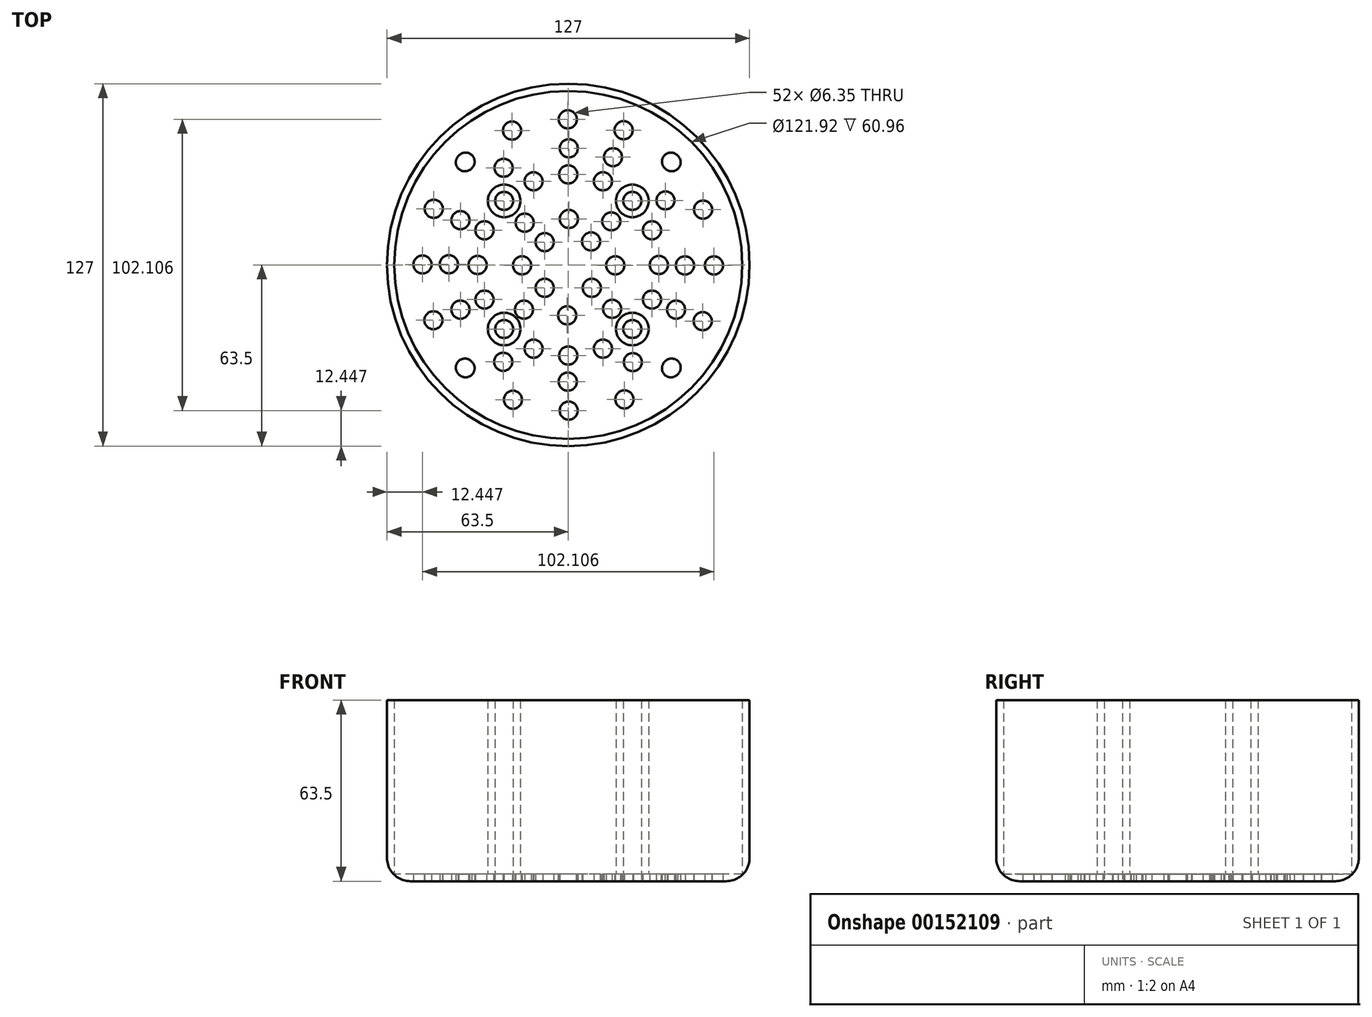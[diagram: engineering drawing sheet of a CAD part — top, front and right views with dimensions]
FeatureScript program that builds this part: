
annotation { "Feature Type Name" : "Feature", "Feature Type Description" : "" }
export const myFeature = defineFeature(function(context is Context, id is Id, definition is map)
    precondition{}
    {
        {
            var Q0;
            Q0=qCreatedBy(makeId("Top.planeOp"),FACE);
            var sketch = newSketch(context, id + "F0", { "sketchPlane" : qUnion([Q0])});
            skCircle(sketch, "E0", {"center": v(0, 0) * mm, "radius": 63.5 * mm});
            skLineSegment(sketch, "E1", {"start": v(0, 0) * mm, "end": v(-63.5, 0) * mm, "construction": true});
            skLineSegment(sketch, "E2", {"start": v(-63.5, 0) * mm, "end": v(0, 0) * mm, "construction": true});
            skLineSegment(sketch, "E3", {"start": v(0, 0) * mm, "end": v(-44.9, 44.9) * mm, "construction": true});
            skCircle(sketch, "E4", {"center": v(-22.45, 22.45) * mm, "radius": 3.18 * mm});
            skCircle(sketch, "E5", {"center": v(-36.22, 35.98) * mm, "radius": 3.18 * mm});
            skCircle(sketch, "E6", {"center": v(-8.25, 8.02) * mm, "radius": 3.18 * mm});
            skCircle(sketch, "E7.MirrorC", {"center": v(-8.25, -8.02) * mm, "radius": 3.18 * mm});
            skCircle(sketch, "E8.MirrorC", {"center": v(-36.22, -35.98) * mm, "radius": 3.18 * mm});
            skCircle(sketch, "E9.MirrorC", {"center": v(-22.45, -22.45) * mm, "radius": 3.18 * mm});
            skCircle(sketch, "E10.MirrorC", {"center": v(8.02, 8.25) * mm, "radius": 3.18 * mm});
            skCircle(sketch, "E11.MirrorC", {"center": v(22.45, 22.45) * mm, "radius": 3.18 * mm});
            skLineSegment(sketch, "E12.MirrorCS", {"start": v(0, 0) * mm, "end": v(-44.9, -44.9) * mm, "construction": true});
            skLineSegment(sketch, "E13.MirrorCS", {"start": v(0, 0) * mm, "end": v(44.9, -44.9) * mm, "construction": true});
            skLineSegment(sketch, "E14.MirrorCS", {"start": v(0, 0) * mm, "end": v(44.9, 44.9) * mm, "construction": true});
            skCircle(sketch, "E15.MirrorC", {"center": v(36.22, 35.98) * mm, "radius": 3.18 * mm});
            skCircle(sketch, "E16.MirrorC", {"center": v(36.22, -35.98) * mm, "radius": 3.18 * mm});
            skCircle(sketch, "E17.MirrorC", {"center": v(22.45, -22.45) * mm, "radius": 3.18 * mm});
            skCircle(sketch, "E18.MirrorC", {"center": v(8.25, -8.02) * mm, "radius": 3.18 * mm});
            skCircle(sketch, "E19.1.0", {"center": v(-19.69, 47.1) * mm, "radius": 3.18 * mm});
            skCircle(sketch, "E19.1.1", {"center": v(-12.15, 29.33) * mm, "radius": 3.18 * mm});
            skCircle(sketch, "E19.1.2", {"center": v(29.33, 12.15) * mm, "radius": 3.18 * mm});
            skCircle(sketch, "E19.1.3", {"center": v(47.23, 19.39) * mm, "radius": 3.18 * mm});
            skCircle(sketch, "E19.1.4", {"center": v(12.15, -29.33) * mm, "radius": 3.18 * mm});
            skCircle(sketch, "E19.1.5", {"center": v(19.69, -47.1) * mm, "radius": 3.18 * mm});
            skCircle(sketch, "E19.1.6", {"center": v(-47.23, -19.39) * mm, "radius": 3.18 * mm});
            skCircle(sketch, "E19.1.7", {"center": v(-29.33, -12.15) * mm, "radius": 3.18 * mm});
            skCircle(sketch, "E19.2.0", {"center": v(-0.16, 51.05) * mm, "radius": 3.18 * mm});
            skCircle(sketch, "E19.2.1", {"center": v(0, 31.75) * mm, "radius": 3.18 * mm});
            skCircle(sketch, "E19.2.2", {"center": v(31.75, 0) * mm, "radius": 3.18 * mm});
            skCircle(sketch, "E19.2.3", {"center": v(51.05, -0.16) * mm, "radius": 3.18 * mm});
            skCircle(sketch, "E19.2.4", {"center": v(0, -31.75) * mm, "radius": 3.18 * mm});
            skCircle(sketch, "E19.2.5", {"center": v(0.16, -51.05) * mm, "radius": 3.18 * mm});
            skCircle(sketch, "E19.2.6", {"center": v(-51.05, 0.16) * mm, "radius": 3.18 * mm});
            skCircle(sketch, "E19.2.7", {"center": v(-31.75, 0) * mm, "radius": 3.18 * mm});
            skLineSegment(sketch, "E19.anchor1", {"start": v(0, 0) * mm, "end": v(-36.22, 35.98) * mm, "construction": true});
            skLineSegment(sketch, "E19.anchor2", {"start": v(0, 0) * mm, "end": v(-0.16, 51.05) * mm, "construction": true});
            skCircle(sketch, "E20.1.0", {"center": v(19.39, 47.23) * mm, "radius": 3.18 * mm});
            skCircle(sketch, "E20.1.1", {"center": v(12.15, 29.33) * mm, "radius": 3.18 * mm});
            skCircle(sketch, "E20.1.2", {"center": v(47.1, -19.69) * mm, "radius": 3.18 * mm});
            skCircle(sketch, "E20.1.3", {"center": v(29.33, -12.15) * mm, "radius": 3.18 * mm});
            skCircle(sketch, "E20.1.4", {"center": v(-12.15, -29.33) * mm, "radius": 3.18 * mm});
            skCircle(sketch, "E20.1.5", {"center": v(-19.39, -47.23) * mm, "radius": 3.18 * mm});
            skCircle(sketch, "E20.1.6", {"center": v(-29.33, 12.15) * mm, "radius": 3.18 * mm});
            skCircle(sketch, "E20.1.7", {"center": v(-47.1, 19.69) * mm, "radius": 3.18 * mm});
            skCircle(sketch, "E20.2.0", {"center": v(35.98, 36.22) * mm, "radius": 3.18 * mm});
            skCircle(sketch, "E20.2.2", {"center": v(35.98, -36.22) * mm, "radius": 3.18 * mm});
            skCircle(sketch, "E20.2.5", {"center": v(-35.98, -36.22) * mm, "radius": 3.18 * mm});
            skCircle(sketch, "E20.2.7", {"center": v(-35.98, 36.22) * mm, "radius": 3.18 * mm});
            skLineSegment(sketch, "E20.anchor2", {"start": v(0, 0) * mm, "end": v(35.98, 36.22) * mm, "construction": true});
            skLineSegment(sketch, "E21", {"start": v(-47.1, 19.69) * mm, "end": v(-29.33, 12.15) * mm});
            skCircle(sketch, "E22.1.7", {"center": v(-37.77, 15.68) * mm, "radius": 3.18 * mm});
            skCircle(sketch, "E23.1.0", {"center": v(-22.63, 34.06) * mm, "radius": 3.18 * mm});
            skCircle(sketch, "E23.2.0", {"center": v(0.18, 40.9) * mm, "radius": 3.18 * mm});
            skLineSegment(sketch, "E23.anchor1", {"start": v(0, 0) * mm, "end": v(-37.77, 15.68) * mm, "construction": true});
            skLineSegment(sketch, "E23.anchor2", {"start": v(0, 0) * mm, "end": v(0.18, 40.9) * mm, "construction": true});
            skCircle(sketch, "E24.1.0", {"center": v(15.68, 37.77) * mm, "radius": 3.18 * mm});
            skCircle(sketch, "E24.1.1", {"center": v(34.06, 22.63) * mm, "radius": 3.18 * mm});
            skCircle(sketch, "E24.1.2", {"center": v(40.9, -0.18) * mm, "radius": 3.18 * mm});
            skCircle(sketch, "E24.2.0", {"center": v(37.77, -15.68) * mm, "radius": 3.18 * mm});
            skCircle(sketch, "E24.2.1", {"center": v(22.63, -34.06) * mm, "radius": 3.18 * mm});
            skCircle(sketch, "E24.2.2", {"center": v(-0.18, -40.9) * mm, "radius": 3.18 * mm});
            skLineSegment(sketch, "E24.anchor2", {"start": v(0, 0) * mm, "end": v(37.77, -15.68) * mm, "construction": true});
            skCircle(sketch, "E25.1.0", {"center": v(-22.8, -33.95) * mm, "radius": 3.18 * mm});
            skCircle(sketch, "E25.2.0", {"center": v(-37.78, -15.65) * mm, "radius": 3.18 * mm});
            skLineSegment(sketch, "E25.anchor1", {"start": v(0, 0) * mm, "end": v(-0.18, -40.9) * mm, "construction": true});
            skLineSegment(sketch, "E25.anchor2", {"start": v(0, 0) * mm, "end": v(-37.78, -15.65) * mm, "construction": true});
            skCircle(sketch, "E26.1.7", {"center": v(-41.83, 0.27) * mm, "radius": 3.18 * mm});
            skCircle(sketch, "E27.1.7", {"center": v(-15.52, -15.68) * mm, "radius": 3.18 * mm});
            skCircle(sketch, "E28.1.7", {"center": v(-0.38, -17.67) * mm, "radius": 3.18 * mm});
            skCircle(sketch, "E29.1.7", {"center": v(15.38, -15.38) * mm, "radius": 3.18 * mm});
            skCircle(sketch, "E30.1.7", {"center": v(16.48, -0.14) * mm, "radius": 3.18 * mm});
            skCircle(sketch, "E31.1.7", {"center": v(15.07, 15.28) * mm, "radius": 3.18 * mm});
            skCircle(sketch, "E32.1.7", {"center": v(0.21, 16.13) * mm, "radius": 3.18 * mm});
            skCircle(sketch, "E33.1.7", {"center": v(-16.2, -0.14) * mm, "radius": 3.18 * mm});
            skCircle(sketch, "E34.1.7", {"center": v(-15.27, 14.8) * mm, "radius": 3.18 * mm});
            skSolve(sketch);
        }
        {
            var Q0;
            Q0=makeQuery(id+"F0.imprint","IMPRINT",FACE,{"disambiguationData":[TD([[makeQuery(id+"F0.imprint","IMPRINT",EDGE,{"derivedFrom":sQuery(id+"F0.wireOp",EDGE,"E0")}),1.0]])]});
            extrude(context, id + "F1", {"entities" : qUnion([Q0]), "depth" : 63.5 * mm});
        }
        {
            var Q0;
            Q0=makeQuery(id+"F1.opExtrude","SWEPT_FACE",FACE,{"disambiguationData":[OSD([sQuery(id+"F0.wireOp",EDGE,"E4")])]});
            var Q1;
            Q1=makeQuery(id+"F1.opExtrude","SWEPT_FACE",FACE,{"disambiguationData":[OSD([sQuery(id+"F0.wireOp",EDGE,"E20.2.7")])]});
            var Q2;
            Q2=makeQuery(id+"F1.opExtrude","SWEPT_FACE",FACE,{"disambiguationData":[OSD([sQuery(id+"F0.wireOp",EDGE,"E19.2.0")])]});
            var Q3;
            Q3=makeQuery(id+"F1.opExtrude","SWEPT_FACE",FACE,{"disambiguationData":[OSD([sQuery(id+"F0.wireOp",EDGE,"E19.1.1")])]});
            var Q4;
            Q4=makeQuery(id+"F1.opExtrude","SWEPT_FACE",FACE,{"disambiguationData":[OSD([sQuery(id+"F0.wireOp",EDGE,"E19.2.1")])]});
            var Q5;
            Q5=makeQuery(id+"F1.opExtrude","SWEPT_FACE",FACE,{"disambiguationData":[OSD([sQuery(id+"F0.wireOp",EDGE,"E20.1.1")])]});
            var Q6;
            Q6=makeQuery(id+"F1.opExtrude","SWEPT_FACE",FACE,{"disambiguationData":[OSD([sQuery(id+"F0.wireOp",EDGE,"E20.1.0")])]});
            var Q7;
            Q7=makeQuery(id+"F1.opExtrude","SWEPT_FACE",FACE,{"disambiguationData":[OSD([sQuery(id+"F0.wireOp",EDGE,"E19.1.0")])]});
            var Q8;
            Q8=makeQuery(id+"F1.opExtrude","SWEPT_FACE",FACE,{"disambiguationData":[OSD([sQuery(id+"F0.wireOp",EDGE,"E5")])]});
            var Q9;
            Q9=makeQuery(id+"F1.opExtrude","SWEPT_FACE",FACE,{"disambiguationData":[OSD([sQuery(id+"F0.wireOp",EDGE,"E20.1.7")])]});
            var Q10;
            Q10=makeQuery(id+"F1.opExtrude","SWEPT_FACE",FACE,{"disambiguationData":[OSD([sQuery(id+"F0.wireOp",EDGE,"E19.2.6")])]});
            var Q11;
            Q11=makeQuery(id+"F1.opExtrude","SWEPT_FACE",FACE,{"disambiguationData":[OSD([sQuery(id+"F0.wireOp",EDGE,"E19.1.6")])]});
            var Q12;
            Q12=makeQuery(id+"F1.opExtrude","SWEPT_FACE",FACE,{"disambiguationData":[OSD([sQuery(id+"F0.wireOp",EDGE,"E19.2.7")])]});
            var Q13;
            Q13=makeQuery(id+"F1.opExtrude","SWEPT_FACE",FACE,{"disambiguationData":[OSD([sQuery(id+"F0.wireOp",EDGE,"E20.1.6")])]});
            var Q14;
            Q14=makeQuery(id+"F1.opExtrude","SWEPT_FACE",FACE,{"disambiguationData":[OSD([sQuery(id+"F0.wireOp",EDGE,"E19.1.7")])]});
            var Q15;
            Q15=makeQuery(id+"F1.opExtrude","SWEPT_FACE",FACE,{"disambiguationData":[OSD([sQuery(id+"F0.wireOp",EDGE,"E9.MirrorC")])]});
            var Q16;
            Q16=makeQuery(id+"F1.opExtrude","SWEPT_FACE",FACE,{"disambiguationData":[OSD([sQuery(id+"F0.wireOp",EDGE,"E20.1.5")])]});
            var Q17;
            Q17=makeQuery(id+"F1.opExtrude","SWEPT_FACE",FACE,{"disambiguationData":[OSD([sQuery(id+"F0.wireOp",EDGE,"E20.1.4")])]});
            var Q18;
            Q18=makeQuery(id+"F1.opExtrude","SWEPT_FACE",FACE,{"disambiguationData":[OSD([sQuery(id+"F0.wireOp",EDGE,"E8.MirrorC")])]});
            var Q19;
            Q19=makeQuery(id+"F1.opExtrude","SWEPT_FACE",FACE,{"disambiguationData":[OSD([sQuery(id+"F0.wireOp",EDGE,"E20.2.5")])]});
            var Q20;
            Q20=makeQuery(id+"F1.opExtrude","SWEPT_FACE",FACE,{"disambiguationData":[OSD([sQuery(id+"F0.wireOp",EDGE,"E7.MirrorC")])]});
            var Q21;
            Q21=makeQuery(id+"F1.opExtrude","SWEPT_FACE",FACE,{"disambiguationData":[OSD([sQuery(id+"F0.wireOp",EDGE,"E6")])]});
            var Q22;
            Q22=makeQuery(id+"F1.opExtrude","SWEPT_FACE",FACE,{"disambiguationData":[OSD([sQuery(id+"F0.wireOp",EDGE,"E10.MirrorC")])]});
            var Q23;
            Q23=makeQuery(id+"F1.opExtrude","SWEPT_FACE",FACE,{"disambiguationData":[OSD([sQuery(id+"F0.wireOp",EDGE,"E18.MirrorC")])]});
            var Q24;
            Q24=makeQuery(id+"F1.opExtrude","SWEPT_FACE",FACE,{"disambiguationData":[OSD([sQuery(id+"F0.wireOp",EDGE,"E20.1.3")])]});
            var Q25;
            Q25=makeQuery(id+"F1.opExtrude","SWEPT_FACE",FACE,{"disambiguationData":[OSD([sQuery(id+"F0.wireOp",EDGE,"E19.2.2")])]});
            var Q26;
            Q26=makeQuery(id+"F1.opExtrude","SWEPT_FACE",FACE,{"disambiguationData":[OSD([sQuery(id+"F0.wireOp",EDGE,"E19.1.2")])]});
            var Q27;
            Q27=makeQuery(id+"F1.opExtrude","SWEPT_FACE",FACE,{"disambiguationData":[OSD([sQuery(id+"F0.wireOp",EDGE,"E11.MirrorC")])]});
            var Q28;
            Q28=makeQuery(id+"F1.opExtrude","CAP_FACE",FACE,{"disambiguationData":[OSD([sQuery(id+"F0.wireOp",EDGE,"E0"),sQuery(id+"F0.wireOp",EDGE,"E6"),sQuery(id+"F0.wireOp",EDGE,"E8.MirrorC"),sQuery(id+"F0.wireOp",EDGE,"E10.MirrorC"),sQuery(id+"F0.wireOp",EDGE,"E7.MirrorC"),sQuery(id+"F0.wireOp",EDGE,"E5"),sQuery(id+"F0.wireOp",EDGE,"E15.MirrorC"),sQuery(id+"F0.wireOp",EDGE,"E16.MirrorC"),sQuery(id+"F0.wireOp",EDGE,"E18.MirrorC"),sQuery(id+"F0.wireOp",EDGE,"E19.1.0"),sQuery(id+"F0.wireOp",EDGE,"E19.1.1"),sQuery(id+"F0.wireOp",EDGE,"E19.1.2"),sQuery(id+"F0.wireOp",EDGE,"E19.1.3"),sQuery(id+"F0.wireOp",EDGE,"E19.1.4"),sQuery(id+"F0.wireOp",EDGE,"E19.1.5"),sQuery(id+"F0.wireOp",EDGE,"E19.1.6"),sQuery(id+"F0.wireOp",EDGE,"E19.1.7"),sQuery(id+"F0.wireOp",EDGE,"E19.2.0"),sQuery(id+"F0.wireOp",EDGE,"E19.2.1"),sQuery(id+"F0.wireOp",EDGE,"E19.2.2"),sQuery(id+"F0.wireOp",EDGE,"E19.2.3"),sQuery(id+"F0.wireOp",EDGE,"E19.2.4"),sQuery(id+"F0.wireOp",EDGE,"E19.2.5"),sQuery(id+"F0.wireOp",EDGE,"E19.2.6"),sQuery(id+"F0.wireOp",EDGE,"E19.2.7"),sQuery(id+"F0.wireOp",EDGE,"E20.1.0"),sQuery(id+"F0.wireOp",EDGE,"E20.1.1"),sQuery(id+"F0.wireOp",EDGE,"E20.1.2"),sQuery(id+"F0.wireOp",EDGE,"E20.1.3"),sQuery(id+"F0.wireOp",EDGE,"E20.1.4"),sQuery(id+"F0.wireOp",EDGE,"E20.1.5"),sQuery(id+"F0.wireOp",EDGE,"E20.1.6"),sQuery(id+"F0.wireOp",EDGE,"E20.1.7"),sQuery(id+"F0.wireOp",EDGE,"E20.2.0"),sQuery(id+"F0.wireOp",EDGE,"E11.MirrorC"),sQuery(id+"F0.wireOp",EDGE,"E20.2.2"),sQuery(id+"F0.wireOp",EDGE,"E17.MirrorC"),sQuery(id+"F0.wireOp",EDGE,"E9.MirrorC"),sQuery(id+"F0.wireOp",EDGE,"E20.2.5"),sQuery(id+"F0.wireOp",EDGE,"E4"),sQuery(id+"F0.wireOp",EDGE,"E20.2.7")])],"isStart":false});
            var Q29;
            Q29=makeQuery(id+"F1.opExtrude","SWEPT_FACE",FACE,{"disambiguationData":[OSD([sQuery(id+"F0.wireOp",EDGE,"E19.1.3")])]});
            var Q30;
            Q30=makeQuery(id+"F1.opExtrude","SWEPT_FACE",FACE,{"disambiguationData":[OSD([sQuery(id+"F0.wireOp",EDGE,"E19.2.3")])]});
            var Q31;
            Q31=makeQuery(id+"F1.opExtrude","SWEPT_FACE",FACE,{"disambiguationData":[OSD([sQuery(id+"F0.wireOp",EDGE,"E20.1.2")])]});
            var Q32;
            Q32=makeQuery(id+"F1.opExtrude","SWEPT_FACE",FACE,{"disambiguationData":[OSD([sQuery(id+"F0.wireOp",EDGE,"E17.MirrorC")])]});
            var Q33;
            Q33=makeQuery(id+"F1.opExtrude","SWEPT_FACE",FACE,{"disambiguationData":[OSD([sQuery(id+"F0.wireOp",EDGE,"E19.1.5")])]});
            var Q34;
            Q34=makeQuery(id+"F1.opExtrude","SWEPT_FACE",FACE,{"disambiguationData":[OSD([sQuery(id+"F0.wireOp",EDGE,"E19.2.4")])]});
            var Q35;
            Q35=makeQuery(id+"F1.opExtrude","SWEPT_FACE",FACE,{"disambiguationData":[OSD([sQuery(id+"F0.wireOp",EDGE,"E19.2.5")])]});
            var Q36;
            Q36=makeQuery(id+"F1.opExtrude","SWEPT_FACE",FACE,{"disambiguationData":[OSD([sQuery(id+"F0.wireOp",EDGE,"E19.1.4")])]});
            var Q37;
            Q37=makeQuery(id+"F1.opExtrude","SWEPT_FACE",FACE,{"disambiguationData":[OSD([sQuery(id+"F0.wireOp",EDGE,"E15.MirrorC")])]});
            var Q38;
            Q38=makeQuery(id+"F1.opExtrude","SWEPT_FACE",FACE,{"disambiguationData":[OSD([sQuery(id+"F0.wireOp",EDGE,"E20.2.0")])]});
            var Q39;
            Q39=makeQuery(id+"F1.opExtrude","SWEPT_FACE",FACE,{"disambiguationData":[OSD([sQuery(id+"F0.wireOp",EDGE,"E20.2.2")])]});
            var Q40;
            Q40=makeQuery(id+"F1.opExtrude","SWEPT_FACE",FACE,{"disambiguationData":[OSD([sQuery(id+"F0.wireOp",EDGE,"E16.MirrorC")])]});
            var Q41;
            Q41=makeQuery(id+"F1.opExtrude","SWEPT_FACE",FACE,{"disambiguationData":[OSD([sQuery(id+"F0.wireOp",EDGE,"E25.1.0")])]});
            var Q42;
            Q42=makeQuery(id+"F1.opExtrude","SWEPT_FACE",FACE,{"disambiguationData":[OSD([sQuery(id+"F0.wireOp",EDGE,"E27.1.7")])]});
            var Q43;
            Q43=makeQuery(id+"F1.opExtrude","SWEPT_FACE",FACE,{"disambiguationData":[OSD([sQuery(id+"F0.wireOp",EDGE,"E24.2.2")])]});
            var Q44;
            Q44=makeQuery(id+"F1.opExtrude","SWEPT_FACE",FACE,{"disambiguationData":[OSD([sQuery(id+"F0.wireOp",EDGE,"E24.2.1")])]});
            var Q45;
            Q45=makeQuery(id+"F1.opExtrude","SWEPT_FACE",FACE,{"disambiguationData":[OSD([sQuery(id+"F0.wireOp",EDGE,"E28.1.7")])]});
            var Q46;
            Q46=makeQuery(id+"F1.opExtrude","SWEPT_FACE",FACE,{"disambiguationData":[OSD([sQuery(id+"F0.wireOp",EDGE,"E29.1.7")])]});
            var Q47;
            Q47=makeQuery(id+"F1.opExtrude","SWEPT_FACE",FACE,{"disambiguationData":[OSD([sQuery(id+"F0.wireOp",EDGE,"E24.2.0")])]});
            var Q48;
            Q48=makeQuery(id+"F1.opExtrude","SWEPT_FACE",FACE,{"disambiguationData":[OSD([sQuery(id+"F0.wireOp",EDGE,"E33.1.7")])]});
            var Q49;
            Q49=makeQuery(id+"F1.opExtrude","SWEPT_FACE",FACE,{"disambiguationData":[OSD([sQuery(id+"F0.wireOp",EDGE,"4bda6821-7396-41a6-ba32-7f5fa97dda8a.1.7")])]});
            var Q50;
            Q50=makeQuery(id+"F1.opExtrude","SWEPT_FACE",FACE,{"disambiguationData":[OSD([sQuery(id+"F0.wireOp",EDGE,"E25.2.0")])]});
            var Q51;
            Q51=makeQuery(id+"F1.opExtrude","SWEPT_FACE",FACE,{"disambiguationData":[OSD([sQuery(id+"F0.wireOp",EDGE,"E26.1.7")])]});
            var Q52;
            Q52=makeQuery(id+"F1.opExtrude","SWEPT_FACE",FACE,{"disambiguationData":[OSD([sQuery(id+"F0.wireOp",EDGE,"E22.1.7")])]});
            var Q53;
            Q53=makeQuery(id+"F1.opExtrude","SWEPT_FACE",FACE,{"disambiguationData":[OSD([sQuery(id+"F0.wireOp",EDGE,"E34.1.7")])]});
            var Q54;
            Q54=makeQuery(id+"F1.opExtrude","SWEPT_FACE",FACE,{"disambiguationData":[OSD([sQuery(id+"F0.wireOp",EDGE,"E23.1.0")])]});
            var Q55;
            Q55=makeQuery(id+"F1.opExtrude","SWEPT_FACE",FACE,{"disambiguationData":[OSD([sQuery(id+"F0.wireOp",EDGE,"E32.1.7")])]});
            var Q56;
            Q56=makeQuery(id+"F1.opExtrude","SWEPT_FACE",FACE,{"disambiguationData":[OSD([sQuery(id+"F0.wireOp",EDGE,"E31.1.7")])]});
            var Q57;
            Q57=makeQuery(id+"F1.opExtrude","SWEPT_FACE",FACE,{"disambiguationData":[OSD([sQuery(id+"F0.wireOp",EDGE,"E30.1.7")])]});
            var Q58;
            Q58=makeQuery(id+"F1.opExtrude","SWEPT_FACE",FACE,{"disambiguationData":[OSD([sQuery(id+"F0.wireOp",EDGE,"E23.2.0")])]});
            var Q59;
            Q59=makeQuery(id+"F1.opExtrude","SWEPT_FACE",FACE,{"disambiguationData":[OSD([sQuery(id+"F0.wireOp",EDGE,"E24.1.0")])]});
            var Q60;
            Q60=makeQuery(id+"F1.opExtrude","SWEPT_FACE",FACE,{"disambiguationData":[OSD([sQuery(id+"F0.wireOp",EDGE,"E24.1.1")])]});
            var Q61;
            Q61=makeQuery(id+"F1.opExtrude","SWEPT_FACE",FACE,{"disambiguationData":[OSD([sQuery(id+"F0.wireOp",EDGE,"E24.1.2")])]});
            shell(context, id + "F2", {"entities" : qUnion([Q0, Q1, Q2, Q3, Q4, Q5, Q6, Q7, Q8, Q9, Q10, Q11, Q12, Q13, Q14, Q15, Q16, Q17, Q18, Q19, Q20, Q21, Q22, Q23, Q24, Q25, Q26, Q27, Q28, Q29, Q30, Q31, Q32, Q33, Q34, Q35, Q36, Q37, Q38, Q39, Q40, Q41, Q42, Q43, Q44, Q45, Q46, Q47, Q48, Q49, Q50, Q51, Q52, Q53, Q54, Q55, Q56, Q57, Q58, Q59, Q60, Q61]), "thickness" : 2.54 * mm});
        }
        {
            var Q0;
            Q0=makeQuery(id+"F1.opExtrude","CAP_EDGE",EDGE,{"disambiguationData":[OSD([sQuery(id+"F0.wireOp",EDGE,"E0")])],"isStart":true});
            fillet(context, id + "F3", {"entities" : qUnion([Q0]), "radius" : 8.13 * mm, "tangentPropagation" : true, "allowEdgeOverflow" : false});
        }
    });
